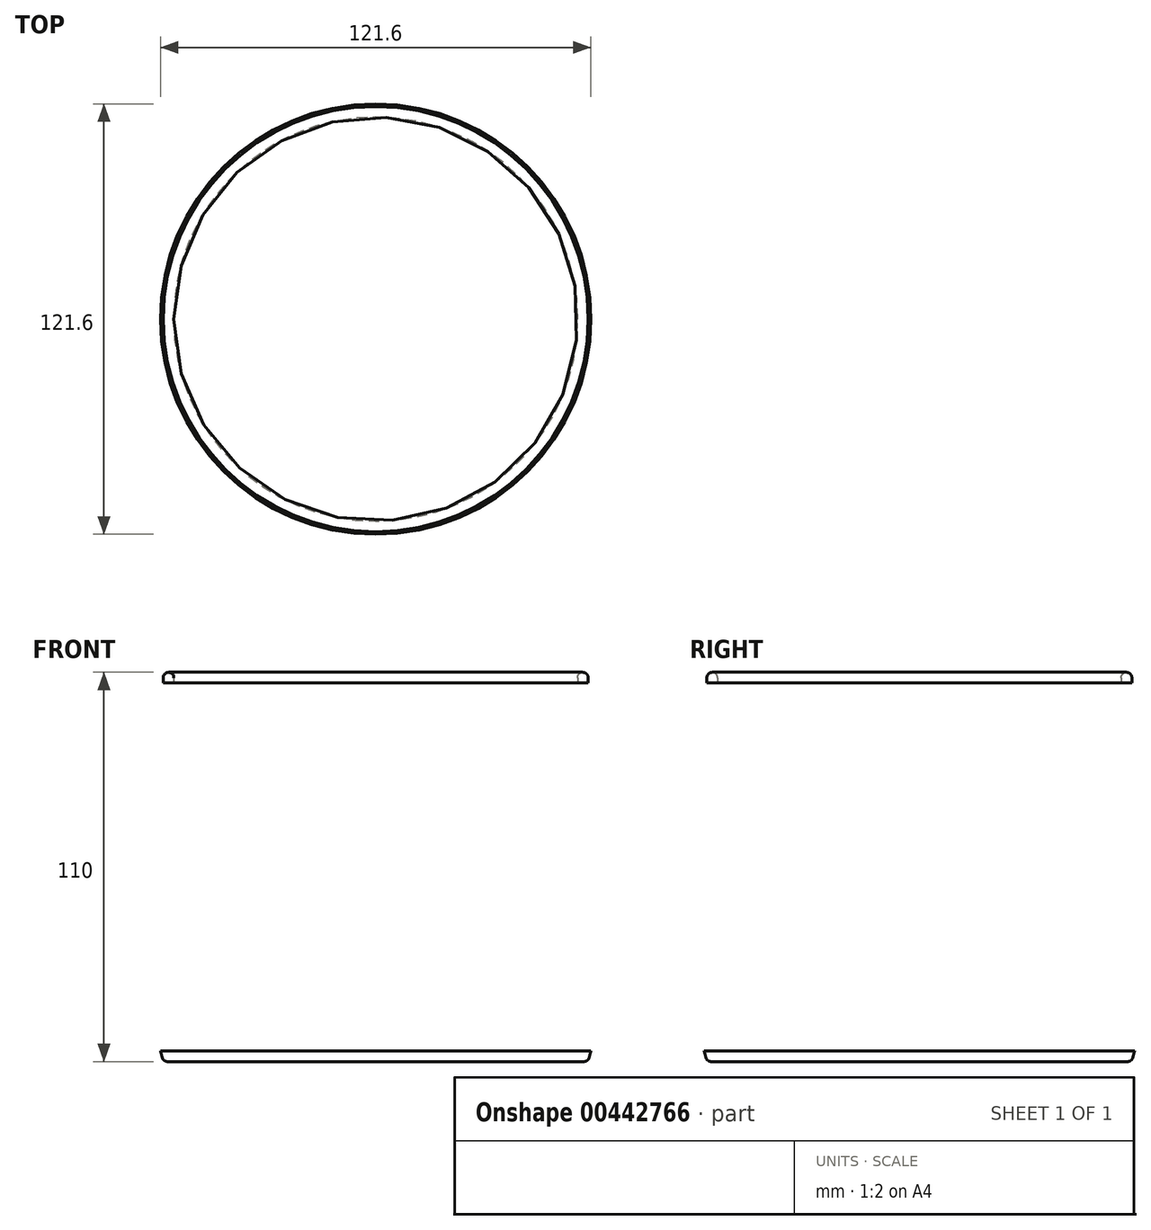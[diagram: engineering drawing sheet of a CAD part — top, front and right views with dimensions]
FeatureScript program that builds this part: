
annotation { "Feature Type Name" : "Feature", "Feature Type Description" : "" }
export const myFeature = defineFeature(function(context is Context, id is Id, definition is map)
    precondition{}
    {
        {
            var Q0;
            Q0=qCreatedBy(makeId("Front.planeOp"),FACE);
            var sketch = newSketch(context, id + "F0", { "sketchPlane" : qUnion([Q0])});
            skLineSegment(sketch, "E0", {"start": v(0, 40.54) * mm, "end": v(-60, 40.54) * mm});
            skLineSegment(sketch, "E1.0", {"start": v(-9, -69.46) * mm, "end": v(-60, -69.46) * mm});
            skLineSegment(sketch, "E2", {"start": v(-9, -69.46) * mm, "end": v(0, -69.46) * mm});
            skLineSegment(sketch, "E3", {"start": v(0, -69.46) * mm, "end": v(0, 40.54) * mm});
            skFitSpline(sketch, "E4", {"points": [v(-60, 40.54) * mm, v(-62.45, 16.46) * mm, v(-61.1, -2.6) * mm, v(-60, -19.93) * mm, v(-63.35, -38.03) * mm, v(-63.3, -51.51) * mm, v(-60, -69.46) * mm], "startDerivative": vector(-3.23, -241.5) * mm, "endDerivative": vector(44.87, -162.11) * mm});
            skSolve(sketch);
        }
        {
            var Q0;
            Q0=makeQuery(id+"F0.imprint","IMPRINT",FACE,{"disambiguationData":[TD([[makeQuery(id+"F0.imprint","IMPRINT",EDGE,{"derivedFrom":sQuery(id+"F0.wireOp",EDGE,"E0")}),1.0]])]});
            var Q1;
            Q1=sQuery(id+"F0.wireOp",EDGE,"E3");
            revolve(context, id + "F1", {"entities" : qUnion([Q0]), "axis" : qUnion([Q1]), "revolveType" : RevolveType.FULL});
        }
        {
            var Q0;
            Q0=makeQuery(id+"F1.opRevolve","SWEPT_FACE",FACE,{"disambiguationData":[OSD([sQuery(id+"F0.wireOp",EDGE,"E0")])]});
            shell(context, id + "F2", {"entities" : qUnion([Q0]), "thickness" : 3 * mm});
        }
        {
            var Q0;
            Q0=qCreatedBy(makeId("Front.planeOp"),FACE);
            var sketch = newSketch(context, id + "F3", { "sketchPlane" : qUnion([Q0])});
            skLineSegment(sketch, "E5.bottom", {"start": v(103.42, -66.46) * mm, "end": v(-96.58, -66.46) * mm});
            skLineSegment(sketch, "E5.top", {"start": v(103.42, 37.54) * mm, "end": v(-96.58, 37.54) * mm});
            skLineSegment(sketch, "E5.left", {"start": v(103.42, -66.46) * mm, "end": v(103.42, 37.54) * mm});
            skLineSegment(sketch, "E5.right", {"start": v(-96.58, -66.46) * mm, "end": v(-96.58, 37.54) * mm});
            skSolve(sketch);
        }
        {
            var Q0;
            Q0 = qSketchRegion(id + "F3", true);
            extrude(context, id + "F4", {"entities" : qUnion([Q0]), "operationType" : NewBodyOperationType.REMOVE, "endBound" : BoundingType.SYMMETRIC, "depth" : 200 * mm});
        }
        {
            var Q0;
            Q0=makeQuery(id+"F1.opRevolve","SWEPT_EDGE",EDGE,{"disambiguationData":[OSD([sQuery(id+"F0.wireOp",EDGE,"E0"),sQuery(id+"F0.wireOp",EDGE,"E4")])]});
            var Q1;
            Q1=makeQuery(id+"F2.opShell","OFFSET_EDGE",EDGE,{"disambiguationData":[OSD([sQuery(id+"F0.wireOp",EDGE,"E0"),sQuery(id+"F0.wireOp",EDGE,"E4")])]});
            var Q2;
            Q2=makeQuery(id+"F1.opRevolve","SWEPT_EDGE",EDGE,{"disambiguationData":[OSD([sQuery(id+"F0.wireOp",EDGE,"E1.0"),sQuery(id+"F0.wireOp",EDGE,"E4")])]});
            fillet(context, id + "F5", {"entities" : qUnion([Q0, Q1, Q2]), "radius" : 1.5 * mm, "tangentPropagation" : true, "allowEdgeOverflow" : false});
        }
    });
